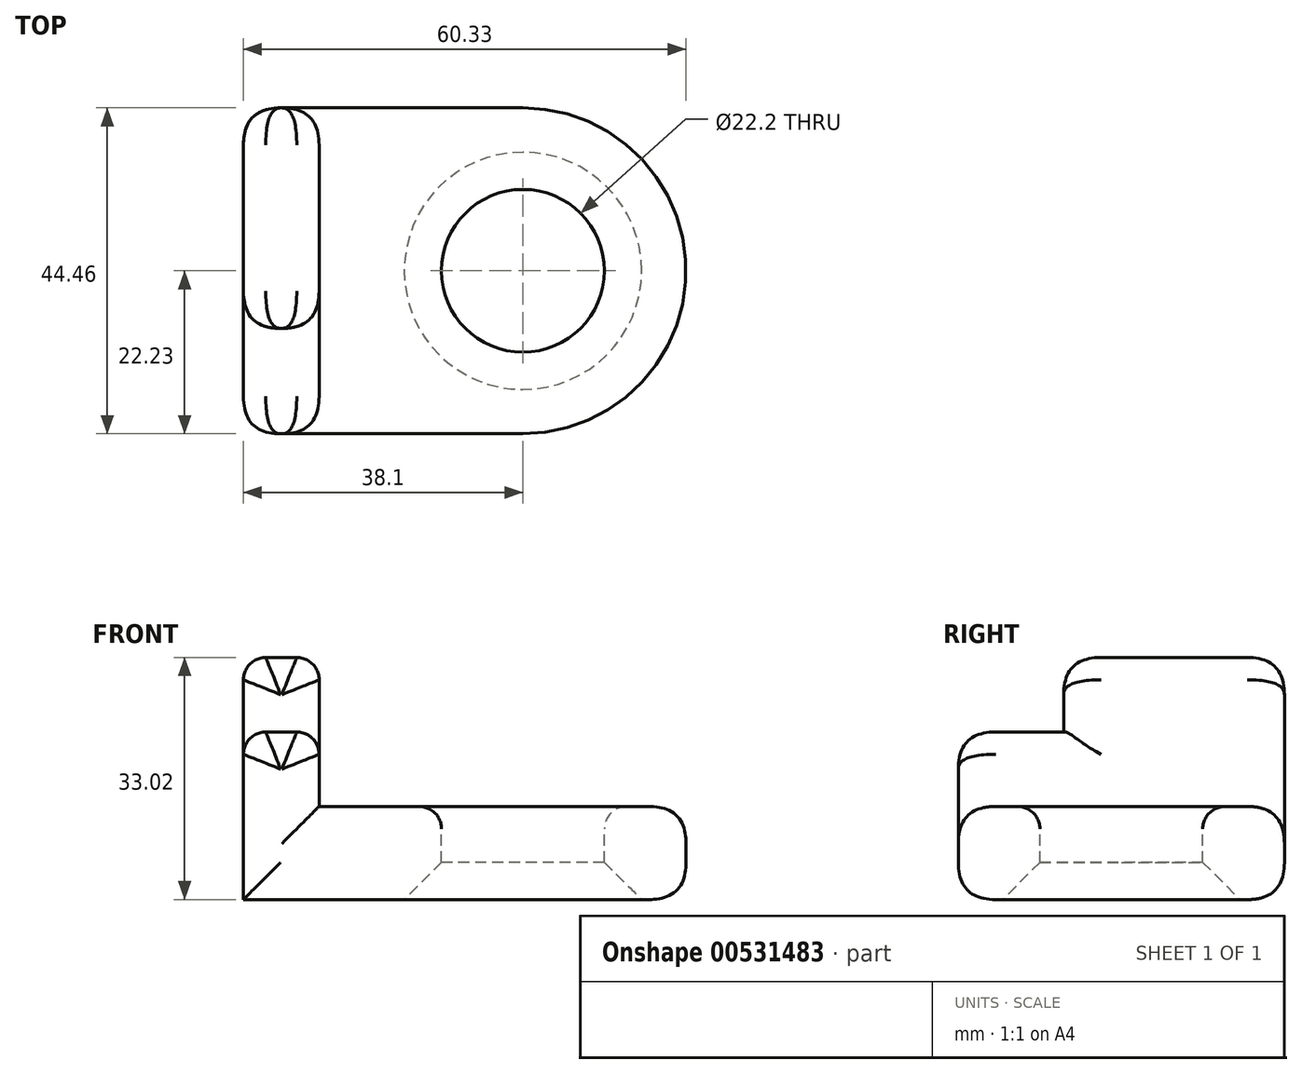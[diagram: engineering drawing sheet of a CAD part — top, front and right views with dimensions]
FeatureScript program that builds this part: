
annotation { "Feature Type Name" : "Feature", "Feature Type Description" : "" }
export const myFeature = defineFeature(function(context is Context, id is Id, definition is map)
    precondition{}
    {
        {
            var Q0;
            Q0=qCreatedBy(makeId("Top.planeOp"),FACE);
            var sketch = newSketch(context, id + "F0", { "sketchPlane" : qUnion([Q0])});
            skLineSegment(sketch, "E0.bottom", {"start": v(19.05, 22.23) * mm, "end": v(-19.05, 22.23) * mm});
            skLineSegment(sketch, "E0.top", {"start": v(19.05, -22.23) * mm, "end": v(-19.05, -22.23) * mm});
            skLineSegment(sketch, "E0.right", {"start": v(-19.05, 22.23) * mm, "end": v(-19.05, -22.22) * mm});
            skPoint(sketch, "E0.middle", {"position": v(0, 0) * mm});
            skArc(sketch, "E1", {"start": v(19.05, -22.22) * mm, "mid": v(41.28, 0) * mm, "end": v(19.05, 22.23) * mm});
            skCircle(sketch, "E2", {"center": v(19.05, 0) * mm, "radius": 11.1 * mm});
            skLineSegment(sketch, "E3", {"start": v(-8.73, 22.23) * mm, "end": v(-8.73, -22.23) * mm});
            skLineSegment(sketch, "E4", {"start": v(-19.05, -7.86) * mm, "end": v(-8.73, -7.86) * mm});
            skSolve(sketch);
        }
        {
            var Q0;
            Q0 = qSketchRegion(id + "F0", true);
            extrude(context, id + "F1", {"entities" : qUnion([Q0]), "oppositeDirection" : true, "depth" : 12.7 * mm, "offsetDistance" : 25.4 * mm});
        }
        {
            var Q0;
            {var subQ0=sQuery(id+"F0.wireOp",EDGE,"E0.right");Q0=makeQuery(id+"F0.imprint","IMPRINT",FACE,{"disambiguationData":[TD([[makeQuery(id+"F0.imprint","IMPRINT",EDGE,{"derivedFrom":subQ0}),1.0]])]});}
            extrude(context, id + "F2", {"entities" : qUnion([Q0]), "operationType" : NewBodyOperationType.ADD, "depth" : 10.16 * mm, "offsetDistance" : 25.4 * mm});
        }
        {
            var Q0;
            {var subQ5=sQuery(id+"F0.wireOp",EDGE,"E4");Q0=makeQuery(id+"F0.imprint","IMPRINT",FACE,{"disambiguationData":[TD([[makeQuery(id+"F0.imprint","IMPRINT",EDGE,{"derivedFrom":subQ5}),1.0]])]});}
            extrude(context, id + "F3", {"entities" : qUnion([Q0]), "operationType" : NewBodyOperationType.ADD, "depth" : 20.32 * mm, "offsetDistance" : 25.4 * mm});
        }
        {
            var Q0;
            Q0=makeQuery(id+"F3.opExtrude","CAP_EDGE",EDGE,{"disambiguationData":[OSD([sQuery(id+"F0.wireOp",EDGE,"E3")])],"isStart":false});
            fillet(context, id + "F4", {"entities" : qUnion([Q0]), "radius" : 3.05 * mm, "tangentPropagation" : true, "allowEdgeOverflow" : false});
        }
        {
            var Q0;
            Q0=makeQuery(id+"F3.opExtrude","CAP_EDGE",EDGE,{"disambiguationData":[OSD([sQuery(id+"F0.wireOp",EDGE,"E0.right")])],"isStart":false});
            fillet(context, id + "F5", {"entities" : qUnion([Q0]), "radius" : 3.05 * mm, "tangentPropagation" : true, "allowEdgeOverflow" : false});
        }
        {
            var Q0;
            Q0=makeQuery(id+"F2.opExtrude","CAP_EDGE",EDGE,{"disambiguationData":[OSD([sQuery(id+"F0.wireOp",EDGE,"E3")])],"isStart":false});
            fillet(context, id + "F6", {"entities" : qUnion([Q0]), "radius" : 3.05 * mm, "tangentPropagation" : true, "allowEdgeOverflow" : false});
        }
        {
            var Q0;
            Q0=makeQuery(id+"F2.opExtrude","CAP_EDGE",EDGE,{"disambiguationData":[OSD([sQuery(id+"F0.wireOp",EDGE,"E0.right")])],"isStart":false});
            var Q1;
            Q1=makeQuery(id+"F1.opExtrude","CAP_EDGE",EDGE,{"disambiguationData":[OSD([sQuery(id+"F0.wireOp",EDGE,"E2")])],"isStart":true});
            fillet(context, id + "F7", {"entities" : qUnion([Q0, Q1]), "radius" : 3.05 * mm, "tangentPropagation" : true, "allowEdgeOverflow" : false});
        }
        {
            var Q0;
            Q0=makeQuery(id+"F1.opExtrude","CAP_EDGE",EDGE,{"disambiguationData":[OSD([sQuery(id+"F0.wireOp",EDGE,"E2")])],"isStart":false});
            chamfer(context, id + "F8", {"entities" : qUnion([Q0]), "width" : 5.08 * mm, "tangentPropagation" : true});
        }
        {
            var Q0;
            Q0=makeQuery(id+"F1.opExtrude","CAP_EDGE",EDGE,{"disambiguationData":[OSD([sQuery(id+"F0.wireOp",EDGE,"E1")])],"isStart":true});
            var Q1;
            Q1=makeQuery(id+"F1.opExtrude","CAP_EDGE",EDGE,{"disambiguationData":[OSD([sQuery(id+"F0.wireOp",EDGE,"E0.top")])],"isStart":false});
            var Q2;
            {var subQ0=sQuery(id+"F0.wireOp",EDGE,"E0.right");var subQ1=sQuery(id+"F0.wireOp",EDGE,"E0.bottom");Q2=makeQuery(id+"F3.boolean.opBoolean","MERGE",EDGE,{"derivedFrom":[makeQuery(id+"F2.boolean.opBoolean","MERGE",EDGE,{"derivedFrom":[makeQuery(id+"F1.opExtrude","SWEPT_EDGE",EDGE,{"disambiguationData":[OSD([subQ1,subQ0])]}),makeQuery(id+"F2.opExtrude","SWEPT_EDGE",EDGE,{"disambiguationData":[OSD([subQ1,subQ0])]})]}),makeQuery(id+"F3.opExtrude","SWEPT_EDGE",EDGE,{"disambiguationData":[OSD([subQ1,subQ0])]})]});}
            var Q3;
            {var subQ0=sQuery(id+"F0.wireOp",EDGE,"E3");var subQ1=sQuery(id+"F0.wireOp",EDGE,"E0.bottom");Q3=makeQuery(id+"F3.boolean.opBoolean","MERGE",EDGE,{"derivedFrom":[makeQuery(id+"F2.opExtrude","SWEPT_EDGE",EDGE,{"disambiguationData":[OSD([subQ1,subQ0])]}),makeQuery(id+"F3.opExtrude","SWEPT_EDGE",EDGE,{"disambiguationData":[OSD([subQ1,subQ0])]})]});}
            var Q4;
            {var subQ0=sQuery(id+"F0.wireOp",EDGE,"E0.right");var subQ1=sQuery(id+"F0.wireOp",EDGE,"E0.top");Q4=makeQuery(id+"F2.boolean.opBoolean","MERGE",EDGE,{"derivedFrom":[makeQuery(id+"F1.opExtrude","SWEPT_EDGE",EDGE,{"disambiguationData":[OSD([subQ1,subQ0])]}),makeQuery(id+"F2.opExtrude","SWEPT_EDGE",EDGE,{"disambiguationData":[OSD([subQ1,subQ0])]})]});}
            var Q5;
            Q5=makeQuery(id+"F2.opExtrude","SWEPT_EDGE",EDGE,{"disambiguationData":[OSD([sQuery(id+"F0.wireOp",EDGE,"E0.top"),sQuery(id+"F0.wireOp",EDGE,"E3")])]});
            var Q6;
            Q6=makeQuery(id+"F3.opExtrude","SWEPT_EDGE",EDGE,{"disambiguationData":[OSD([sQuery(id+"F0.wireOp",EDGE,"E3"),sQuery(id+"F0.wireOp",EDGE,"E4")])]});
            fillet(context, id + "F9", {"entities" : qUnion([Q0, Q1, Q2, Q3, Q4, Q5, Q6]), "radius" : 5.08 * mm, "tangentPropagation" : true, "rho" : 0.5, "crossSection" : FilletCrossSection.CONIC, "allowEdgeOverflow" : false});
        }
    });
